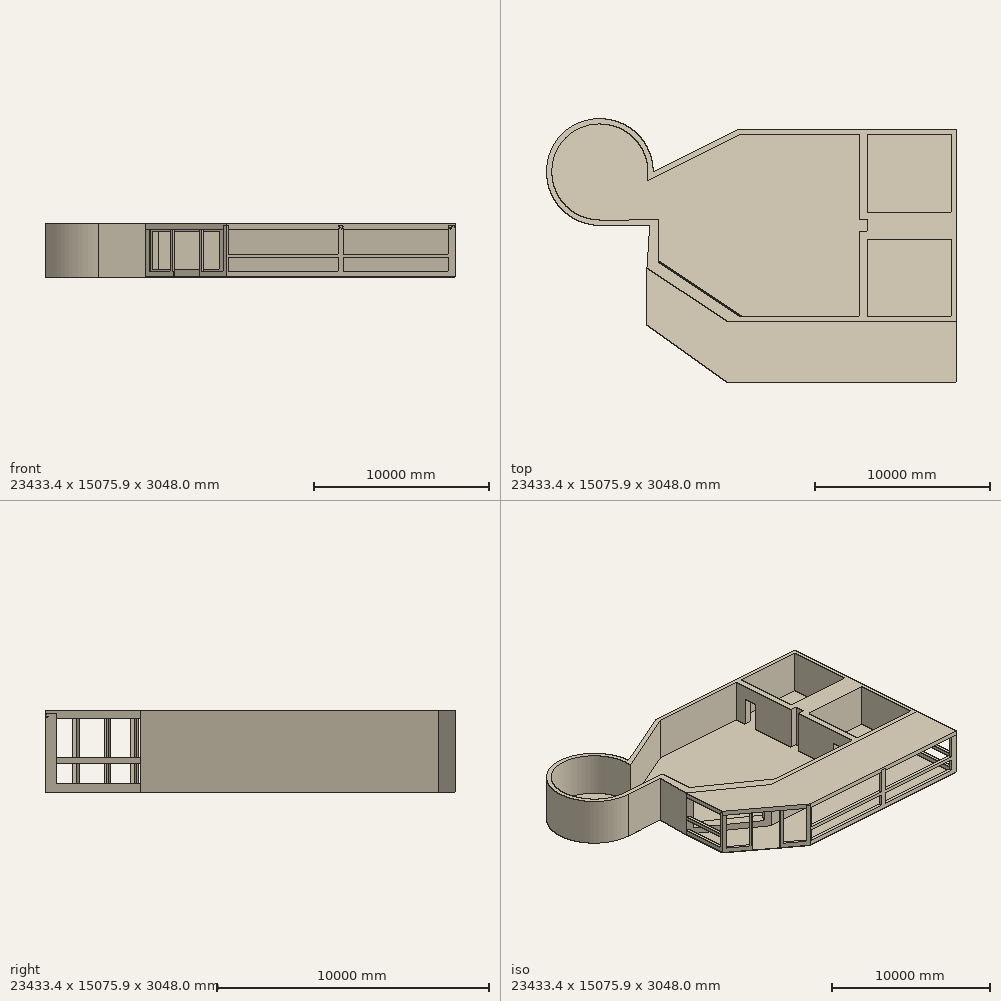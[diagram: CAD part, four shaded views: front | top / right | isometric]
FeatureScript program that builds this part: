
annotation { "Feature Type Name" : "Feature", "Feature Type Description" : "" }
export const myFeature = defineFeature(function(context is Context, id is Id, definition is map)
    precondition{}
    {
        {
            var Q0;
            Q0=qCreatedBy(makeId("Top.planeOp"),FACE);
            var sketch = newSketch(context, id + "F0", { "sketchPlane" : qUnion([Q0])});
            skArc(sketch, "E0", {"start": v(3050.46, 1.82) * mm, "mid": v(-2159.4, 2154.62) * mm, "end": v(4.93, -3050.46) * mm});
            skLineSegment(sketch, "E1", {"start": v(0, -3050.47) * mm, "end": v(2848.18, -3048.16) * mm});
            skPoint(sketch, "E2.start.orphan", {"position": v(-3048, 0) * mm});
            skLineSegment(sketch, "E3.2", {"start": v(7272.16, -8535.97) * mm, "end": v(2693.36, -5490.75) * mm});
            skLineSegment(sketch, "E3.3", {"start": v(2693.36, -5490.75) * mm, "end": v(2848.18, -3048.16) * mm});
            skLineSegment(sketch, "E3.4", {"start": v(3041.2, -2.78) * mm, "end": v(7967.84, 2439.97) * mm});
            skPoint(sketch, "E3.0.midPoint", {"position": v(12372.72, -3349.24) * mm});
            skLineSegment(sketch, "E4", {"start": v(7967.84, 2439.97) * mm, "end": v(20382.9, 2439.97) * mm});
            skLineSegment(sketch, "E5", {"start": v(20382.9, 2439.97) * mm, "end": v(20382.9, -8535.97) * mm});
            skLineSegment(sketch, "E6", {"start": v(20382.9, -8535.97) * mm, "end": v(7272.16, -8535.97) * mm});
            skPoint(sketch, "E7.orphan", {"position": v(12546.64, -605.25) * mm});
            skPoint(sketch, "E3.1.start.orphan", {"position": v(12198.8, -6093.22) * mm});
            skSolve(sketch);
        }
        {
            var Q0;
            Q0 = qSketchRegion(id + "F0", true);
            extrude(context, id + "F1", {"entities" : qUnion([Q0]), "depth" : 3048 * mm, "offsetDistance" : 30.48 * mm});
        }
        {
            var Q0;
            Q0=makeQuery(id+"F1.opExtrude","CAP_FACE",FACE,{"disambiguationData":[OSD([sQuery(id+"F0.wireOp",EDGE,"E0"),sQuery(id+"F0.wireOp",EDGE,"E1"),sQuery(id+"F0.wireOp",EDGE,"E3.2"),sQuery(id+"F0.wireOp",EDGE,"E3.3"),sQuery(id+"F0.wireOp",EDGE,"E3.4"),sQuery(id+"F0.wireOp",EDGE,"E4"),sQuery(id+"F0.wireOp",EDGE,"E5"),sQuery(id+"F0.wireOp",EDGE,"E6")])],"isStart":false});
            var sketch = newSketch(context, id + "F2", { "sketchPlane" : qUnion([Q0])});
            skCircle(sketch, "E8", {"center": v(0, 0) * mm, "radius": 2745.67 * mm});
            skLineSegment(sketch, "E9", {"start": v(2697.21, -513.54) * mm, "end": v(8039.25, 2135.17) * mm});
            skLineSegment(sketch, "E10", {"start": v(8039.25, 2135.17) * mm, "end": v(20078.1, 2135.17) * mm});
            skLineSegment(sketch, "E11", {"start": v(20078.1, 2135.17) * mm, "end": v(20078.1, -8231.17) * mm});
            skLineSegment(sketch, "E12", {"start": v(20078.1, -8231.17) * mm, "end": v(7967.84, -8231.17) * mm});
            skLineSegment(sketch, "E13", {"start": v(7967.84, -8231.17) * mm, "end": v(3324.87, -5143.27) * mm});
            skLineSegment(sketch, "E14", {"start": v(3324.87, -5143.27) * mm, "end": v(3324.87, -2742.98) * mm});
            skLineSegment(sketch, "E15", {"start": v(3324.87, -2742.98) * mm, "end": v(4.93, -2745.66) * mm});
            skSolve(sketch);
        }
        {
            var Q0;
            {var subQ0=sQuery(id+"F2.wireOp",EDGE,"E9");Q0=makeQuery(id+"F2.imprint","IMPRINT",FACE,{"disambiguationData":[TD([[makeQuery(id+"F2.imprint","IMPRINT",EDGE,{"derivedFrom":subQ0}),-1.0]])]});}
            var Q1;
            {var subQ0=sQuery(id+"F2.wireOp",EDGE,"E8");var subQ1=makeQuery(id+"F2.imprint","INTERSECT",VERTEX,{"derivedFrom":[subQ0,sQuery(id+"F2.wireOp",EDGE,"E9")]});Q1=makeQuery(id+"F2.imprint","IMPRINT",FACE,{"disambiguationData":[TD([[makeQuery(id+"F2.imprint","IMPRINT",EDGE,{"disambiguationData":[TD([[subQ1,1.0]])],"derivedFrom":subQ0}),1.0]])]});}
            extrude(context, id + "F3", {"entities" : qUnion([Q0, Q1]), "operationType" : NewBodyOperationType.REMOVE, "oppositeDirection" : true, "depth" : 2743.2 * mm, "offsetDistance" : 30.48 * mm});
        }
        {
            var Q0;
            Q0=makeQuery(id+"F1.opExtrude","SWEPT_FACE",FACE,{"disambiguationData":[OSD([sQuery(id+"F0.wireOp",EDGE,"E3.2")])]});
            var sketch = newSketch(context, id + "F4", { "sketchPlane" : qUnion([Q0])});
            skLineSegment(sketch, "E16.bottom", {"start": v(5740.52, 2590.8) * mm, "end": v(10325.1, 2590.8) * mm});
            skLineSegment(sketch, "E16.top", {"start": v(5740.52, 457.2) * mm, "end": v(10325.1, 457.2) * mm});
            skLineSegment(sketch, "E16.left", {"start": v(5740.52, 2590.8) * mm, "end": v(5740.52, 457.2) * mm});
            skLineSegment(sketch, "E16.right", {"start": v(10325.1, 2590.8) * mm, "end": v(10325.1, 457.2) * mm});
            skSolve(sketch);
        }
        {
            var Q0;
            Q0 = qSketchRegion(id + "F4", true);
            extrude(context, id + "F5", {"entities" : qUnion([Q0]), "operationType" : NewBodyOperationType.REMOVE, "oppositeDirection" : true, "depth" : 914.4 * mm, "offsetDistance" : 30.48 * mm});
        }
        {
            var Q0;
            Q0=makeQuery(id+"F3.boolean.opBoolean","COPY",FACE,{"derivedFrom":makeQuery(id+"F3.opExtrude","SWEPT_FACE",FACE,{"disambiguationData":[OSD([sQuery(id+"F2.wireOp",EDGE,"E13")])]})});
            var sketch = newSketch(context, id + "F6", { "sketchPlane" : qUnion([Q0])});
            skLineSegment(sketch, "E17.bottom", {"start": v(-5616.74, 304.8) * mm, "end": v(-11192.78, 304.8) * mm});
            skLineSegment(sketch, "E17.top", {"start": v(-5616.74, 457.2) * mm, "end": v(-11192.78, 457.2) * mm});
            skLineSegment(sketch, "E17.left", {"start": v(-5616.74, 304.8) * mm, "end": v(-5616.74, 457.2) * mm});
            skLineSegment(sketch, "E17.right", {"start": v(-11192.78, 304.8) * mm, "end": v(-11192.78, 457.2) * mm});
            skSolve(sketch);
        }
        {
            var Q0;
            Q0 = qSketchRegion(id + "F6", true);
            extrude(context, id + "F7", {"entities" : qUnion([Q0]), "operationType" : NewBodyOperationType.ADD, "depth" : 60.96 * mm, "offsetDistance" : 30.48 * mm});
        }
        {
            var Q0;
            Q0=makeQuery(id+"F7.opExtrude","SWEPT_FACE",FACE,{"disambiguationData":[OSD([sQuery(id+"F6.wireOp",EDGE,"E17.right")])]});
            var sketch = newSketch(context, id + "F8", { "sketchPlane" : qUnion([Q0])});
            skLineSegment(sketch, "E18.bottom", {"start": v(-2380.41, 457.2) * mm, "end": v(-2441.37, 457.2) * mm});
            skLineSegment(sketch, "E18.top", {"start": v(-2380.41, 304.8) * mm, "end": v(-2441.37, 304.8) * mm});
            skLineSegment(sketch, "E18.left", {"start": v(-2380.41, 457.2) * mm, "end": v(-2380.41, 304.8) * mm});
            skLineSegment(sketch, "E18.right", {"start": v(-2441.37, 457.2) * mm, "end": v(-2441.37, 304.8) * mm});
            skSolve(sketch);
        }
        {
            var Q0;
            Q0 = qSketchRegion(id + "F8", true);
            extrude(context, id + "F9", {"entities" : qUnion([Q0]), "operationType" : NewBodyOperationType.ADD, "depth" : 91.44 * mm, "offsetDistance" : 30.48 * mm});
        }
        {
            var Q0;
            Q0=makeQuery(id+"F1.opExtrude","CAP_FACE",FACE,{"disambiguationData":[OSD([sQuery(id+"F0.wireOp",EDGE,"E0"),sQuery(id+"F0.wireOp",EDGE,"E1"),sQuery(id+"F0.wireOp",EDGE,"E3.2"),sQuery(id+"F0.wireOp",EDGE,"E3.3"),sQuery(id+"F0.wireOp",EDGE,"E3.4"),sQuery(id+"F0.wireOp",EDGE,"E4"),sQuery(id+"F0.wireOp",EDGE,"E5"),sQuery(id+"F0.wireOp",EDGE,"E6")])],"isStart":true});
            var sketch = newSketch(context, id + "F10", { "sketchPlane" : qUnion([Q0])});
            skLineSegment(sketch, "E19.top", {"start": v(7272.16, 12025.4) * mm, "end": v(20382.9, 12025.4) * mm});
            skLineSegment(sketch, "E19.left", {"start": v(2693.36, 5490.75) * mm, "end": v(2693.36, 8758.07) * mm});
            skLineSegment(sketch, "E19.right", {"start": v(20382.9, 8535.97) * mm, "end": v(20382.9, 12025.4) * mm});
            skLineSegment(sketch, "E20", {"start": v(2693.36, 5490.75) * mm, "end": v(7272.16, 8535.97) * mm});
            skLineSegment(sketch, "E21", {"start": v(7272.16, 8535.97) * mm, "end": v(20382.9, 8535.97) * mm});
            skLineSegment(sketch, "E22", {"start": v(2693.36, 8758.07) * mm, "end": v(7272.16, 12025.4) * mm});
            skPoint(sketch, "E23.orphan", {"position": v(2693.36, 12025.4) * mm});
            skSolve(sketch);
        }
        {
            var Q0;
            Q0 = qSketchRegion(id + "F10", true);
            extrude(context, id + "F11", {"entities" : qUnion([Q0]), "oppositeDirection" : true, "depth" : 30.48 * mm, "offsetDistance" : 30.48 * mm});
        }
        {
            var Q0;
            Q0=makeQuery(id+"F11.opExtrude","CAP_FACE",FACE,{"disambiguationData":[OSD([sQuery(id+"F10.wireOp",EDGE,"E19.top"),sQuery(id+"F10.wireOp",EDGE,"E19.left"),sQuery(id+"F10.wireOp",EDGE,"E19.right"),sQuery(id+"F10.wireOp",EDGE,"E20"),sQuery(id+"F10.wireOp",EDGE,"E21"),sQuery(id+"F10.wireOp",EDGE,"E22")])],"isStart":false});
            var sketch = newSketch(context, id + "F12", { "sketchPlane" : qUnion([Q0])});
            skLineSegment(sketch, "E24", {"start": v(7272.16, -11812.03) * mm, "end": v(20169.55, -11812.03) * mm});
            skLineSegment(sketch, "E25", {"start": v(20169.55, -11812.03) * mm, "end": v(20169.55, -8535.97) * mm});
            skLineSegment(sketch, "E26", {"start": v(2906.72, -5632.65) * mm, "end": v(2906.72, -8696.96) * mm});
            skLineSegment(sketch, "E27", {"start": v(2906.72, -8696.96) * mm, "end": v(7272.16, -11812.03) * mm});
            skSolve(sketch);
        }
        {
            var Q0;
            Q0 = qSketchRegion(id + "F12", true);
            var Q1;
            Q1=makeQuery(id+"F12.imprint","IMPRINT",FACE,{"disambiguationData":[TD([[makeQuery(id+"F12.imprint","IMPRINT",EDGE,{"derivedFrom":sQuery(id+"F12.wireOp",EDGE,"E24")}),-1.0]])]});
            extrude(context, id + "F13", {"entities" : qUnion([Q0, Q1]), "depth" : 304.8 * mm, "offsetDistance" : 30.48 * mm});
        }
        {
            var Q0;
            Q0=makeQuery(id+"F13.opExtrude","SWEPT_FACE",FACE,{"disambiguationData":[OSD([sQuery(id+"F10.wireOp",EDGE,"E22")])]});
            var sketch = newSketch(context, id + "F14", { "sketchPlane" : qUnion([Q0])});
            skLineSegment(sketch, "E28.bottom", {"start": v(10959.47, 30.48) * mm, "end": v(9224.72, 30.48) * mm});
            skLineSegment(sketch, "E28.top", {"start": v(10959.47, 640.08) * mm, "end": v(9224.72, 640.08) * mm});
            skLineSegment(sketch, "E28.left", {"start": v(10959.47, 30.48) * mm, "end": v(10959.47, 640.08) * mm});
            skLineSegment(sketch, "E28.right", {"start": v(9224.72, 30.48) * mm, "end": v(9224.72, 640.08) * mm});
            skPoint(sketch, "E28.middle", {"position": v(10092.1, 335.28) * mm});
            skSolve(sketch);
        }
        {
            var Q0;
            Q0 = qSketchRegion(id + "F14", true);
            extrude(context, id + "F15", {"entities" : qUnion([Q0]), "operationType" : NewBodyOperationType.REMOVE, "oppositeDirection" : true, "depth" : 609.6 * mm, "offsetDistance" : 30.48 * mm});
        }
        {
            var Q0;
            Q0=makeQuery(id+"F15.boolean.opBoolean","COPY",EDGE,{"derivedFrom":makeQuery(id+"F15.opExtrude","CAP_EDGE",EDGE,{"disambiguationData":[OSD([sQuery(id+"F14.wireOp",EDGE,"E28.right")])],"isStart":true})});
            var Q1;
            Q1=makeQuery(id+"F15.boolean.opBoolean","INTERSECT",EDGE,{"derivedFrom":[makeQuery(id+"F13.opExtrude","SWEPT_FACE",FACE,{"disambiguationData":[OSD([sQuery(id+"F12.wireOp",EDGE,"E27")])]}),makeQuery(id+"F15.opExtrude","SWEPT_FACE",FACE,{"disambiguationData":[OSD([sQuery(id+"F14.wireOp",EDGE,"E28.right")])]})]});
            var Q2;
            Q2=makeQuery(id+"F15.boolean.opBoolean","COPY",EDGE,{"derivedFrom":makeQuery(id+"F15.opExtrude","CAP_EDGE",EDGE,{"disambiguationData":[OSD([sQuery(id+"F14.wireOp",EDGE,"E28.left")])],"isStart":true})});
            var Q3;
            Q3=makeQuery(id+"F15.boolean.opBoolean","INTERSECT",EDGE,{"derivedFrom":[makeQuery(id+"F13.opExtrude","SWEPT_FACE",FACE,{"disambiguationData":[OSD([sQuery(id+"F12.wireOp",EDGE,"E27")])]}),makeQuery(id+"F15.opExtrude","SWEPT_FACE",FACE,{"disambiguationData":[OSD([sQuery(id+"F14.wireOp",EDGE,"E28.left")])]})]});
            chamfer(context, id + "F16", {"entities" : qUnion([Q0, Q1, Q2, Q3]), "width" : 60.96 * mm, "tangentPropagation" : true});
        }
        {
            var Q0;
            {var subQ0=sQuery(id+"F10.wireOp",EDGE,"E19.left");var subQ1=sQuery(id+"F12.wireOp",EDGE,"E27");var subQ2=sQuery(id+"F10.wireOp",EDGE,"E22");var subQ3=sQuery(id+"F12.wireOp",EDGE,"E26");var subQ4=sQuery(id+"F10.wireOp",EDGE,"E20");Q0=makeQuery(id+"F15.boolean.opBoolean","SPLIT",FACE,{"disambiguationData":[TD([makeQuery(id+"F13.opExtrude","SWEPT_FACE",FACE,{"disambiguationData":[OSD([subQ3])]})])],"derivedFrom":makeQuery(id+"F13.opExtrude","CAP_FACE",FACE,{"disambiguationData":[OSD([sQuery(id+"F10.wireOp",EDGE,"E19.top"),subQ0,sQuery(id+"F10.wireOp",EDGE,"E19.right"),subQ4,sQuery(id+"F10.wireOp",EDGE,"E21"),subQ2,sQuery(id+"F12.wireOp",EDGE,"E24"),sQuery(id+"F12.wireOp",EDGE,"E25"),subQ3,subQ1])],"isStart":false})});}
            var sketch = newSketch(context, id + "F17", { "sketchPlane" : qUnion([Q0])});
            skLineSegment(sketch, "E29", {"start": v(2906.72, -8600.91) * mm, "end": v(2693.36, -8600.91) * mm});
            skLineSegment(sketch, "E30", {"start": v(2976.84, -8747) * mm, "end": v(2875.95, -8888.37) * mm});
            skLineSegment(sketch, "E31", {"start": v(2875.95, -8888.37) * mm, "end": v(2693.36, -8758.07) * mm});
            skLineSegment(sketch, "E32", {"start": v(2693.36, -8758.07) * mm, "end": v(2693.36, -8600.91) * mm});
            skLineSegment(sketch, "E33", {"start": v(2906.72, -8600.91) * mm, "end": v(2906.72, -8696.96) * mm});
            skLineSegment(sketch, "E34", {"start": v(2906.72, -8696.96) * mm, "end": v(2976.84, -8747) * mm});
            skLineSegment(sketch, "E35", {"start": v(4103.04, -9763.98) * mm, "end": v(4203.92, -9622.6) * mm});
            skLineSegment(sketch, "E36", {"start": v(4203.92, -9622.6) * mm, "end": v(4327.97, -9711.13) * mm});
            skLineSegment(sketch, "E37", {"start": v(4327.97, -9711.13) * mm, "end": v(4342.18, -9796.16) * mm});
            skLineSegment(sketch, "E38", {"start": v(4342.18, -9796.16) * mm, "end": v(4312.12, -9838.29) * mm});
            skLineSegment(sketch, "E39", {"start": v(4312.12, -9838.29) * mm, "end": v(4227.1, -9852.5) * mm});
            skLineSegment(sketch, "E40", {"start": v(4227.1, -9852.5) * mm, "end": v(4103.04, -9763.98) * mm});
            skSolve(sketch);
        }
        {
            var Q0;
            Q0 = qSketchRegion(id + "F17", true);
            extrude(context, id + "F18", {"entities" : qUnion([Q0]), "operationType" : NewBodyOperationType.ADD, "depth" : 2590.8 * mm, "offsetDistance" : 30.48 * mm});
        }
        {
            var Q0;
            {var subQ0=sQuery(id+"F10.wireOp",EDGE,"E19.top");var subQ1=sQuery(id+"F12.wireOp",EDGE,"E25");var subQ2=sQuery(id+"F12.wireOp",EDGE,"E27");var subQ3=sQuery(id+"F12.wireOp",EDGE,"E24");var subQ4=sQuery(id+"F10.wireOp",EDGE,"E21");var subQ5=sQuery(id+"F10.wireOp",EDGE,"E19.right");var subQ6=sQuery(id+"F10.wireOp",EDGE,"E22");Q0=makeQuery(id+"F15.boolean.opBoolean","SPLIT",FACE,{"disambiguationData":[TD([makeQuery(id+"F13.opExtrude","SWEPT_FACE",FACE,{"disambiguationData":[OSD([subQ3])]})])],"derivedFrom":makeQuery(id+"F13.opExtrude","CAP_FACE",FACE,{"disambiguationData":[OSD([subQ0,sQuery(id+"F10.wireOp",EDGE,"E19.left"),subQ5,sQuery(id+"F10.wireOp",EDGE,"E20"),subQ4,subQ6,subQ3,subQ1,sQuery(id+"F12.wireOp",EDGE,"E26"),subQ2])],"isStart":false})});}
            var sketch = newSketch(context, id + "F19", { "sketchPlane" : qUnion([Q0])});
            skLineSegment(sketch, "E41", {"start": v(5963.37, -10878.1) * mm, "end": v(5862.49, -11019.48) * mm});
            skLineSegment(sketch, "E42", {"start": v(5862.49, -11019.48) * mm, "end": v(5738.43, -10930.96) * mm});
            skLineSegment(sketch, "E43", {"start": v(5738.43, -10930.96) * mm, "end": v(5724.22, -10845.93) * mm});
            skLineSegment(sketch, "E44", {"start": v(5724.22, -10845.93) * mm, "end": v(5754.28, -10803.8) * mm});
            skLineSegment(sketch, "E45", {"start": v(5754.28, -10803.8) * mm, "end": v(5839.31, -10789.58) * mm});
            skLineSegment(sketch, "E46", {"start": v(5839.31, -10789.58) * mm, "end": v(5963.37, -10878.1) * mm});
            skLineSegment(sketch, "E47", {"start": v(7201.78, -11761.8) * mm, "end": v(7100.9, -11903.18) * mm});
            skLineSegment(sketch, "E48", {"start": v(7100.9, -11903.18) * mm, "end": v(7272.16, -12025.4) * mm});
            skLineSegment(sketch, "E49", {"start": v(7272.16, -12025.4) * mm, "end": v(7382.18, -12025.4) * mm});
            skLineSegment(sketch, "E50", {"start": v(7382.18, -12025.4) * mm, "end": v(7382.18, -11812.03) * mm});
            skLineSegment(sketch, "E51", {"start": v(7382.18, -11812.03) * mm, "end": v(7272.16, -11812.03) * mm});
            skLineSegment(sketch, "E52", {"start": v(7272.16, -11812.03) * mm, "end": v(7201.78, -11761.8) * mm});
            skLineSegment(sketch, "E53", {"start": v(19960.46, -11812.03) * mm, "end": v(19960.46, -12025.4) * mm});
            skLineSegment(sketch, "E54", {"start": v(19960.46, -12025.4) * mm, "end": v(20382.9, -12025.4) * mm});
            skLineSegment(sketch, "E55", {"start": v(20382.9, -12025.4) * mm, "end": v(20382.9, -11633.8) * mm});
            skLineSegment(sketch, "E56", {"start": v(20382.9, -11633.8) * mm, "end": v(20169.55, -11633.8) * mm});
            skLineSegment(sketch, "E57", {"start": v(20169.55, -11633.8) * mm, "end": v(20169.55, -11812.03) * mm});
            skLineSegment(sketch, "E58", {"start": v(20169.55, -11812.03) * mm, "end": v(19960.46, -11812.03) * mm});
            skLineSegment(sketch, "E59", {"start": v(13827.54, -12025.4) * mm, "end": v(13668.18, -12025.4) * mm});
            skLineSegment(sketch, "E60", {"start": v(13668.18, -12025.4) * mm, "end": v(13668.18, -11812.03) * mm});
            skLineSegment(sketch, "E61", {"start": v(13668.18, -11812.03) * mm, "end": v(13985.48, -11812.03) * mm});
            skLineSegment(sketch, "E62", {"start": v(13985.48, -11812.03) * mm, "end": v(13985.48, -12025.4) * mm});
            skLineSegment(sketch, "E63", {"start": v(13985.48, -12025.4) * mm, "end": v(13827.54, -12025.4) * mm});
            skSolve(sketch);
        }
        {
            var Q0;
            Q0=makeQuery(id+"F19.imprint","IMPRINT",FACE,{"disambiguationData":[TD([[makeQuery(id+"F19.imprint","IMPRINT",EDGE,{"derivedFrom":sQuery(id+"F19.wireOp",EDGE,"E59")}),1.0]])]});
            var Q1;
            Q1=makeQuery(id+"F19.imprint","IMPRINT",FACE,{"disambiguationData":[TD([[makeQuery(id+"F19.imprint","IMPRINT",EDGE,{"derivedFrom":sQuery(id+"F19.wireOp",EDGE,"E53")}),1.0]])]});
            var Q2;
            Q2=makeQuery(id+"F19.imprint","IMPRINT",FACE,{"disambiguationData":[TD([[makeQuery(id+"F19.imprint","IMPRINT",EDGE,{"derivedFrom":sQuery(id+"F19.wireOp",EDGE,"E41")}),-1.0]])]});
            var Q3;
            Q3=makeQuery(id+"F19.imprint","IMPRINT",FACE,{"disambiguationData":[TD([[makeQuery(id+"F19.imprint","IMPRINT",EDGE,{"derivedFrom":sQuery(id+"F19.wireOp",EDGE,"E47")}),1.0]])]});
            extrude(context, id + "F20", {"entities" : qUnion([Q0, Q1, Q2, Q3]), "operationType" : NewBodyOperationType.ADD, "depth" : 2590.8 * mm, "offsetDistance" : 30.48 * mm});
        }
        {
            var Q0;
            Q0=makeQuery(id+"F1.opExtrude","CAP_FACE",FACE,{"disambiguationData":[OSD([sQuery(id+"F0.wireOp",EDGE,"E0"),sQuery(id+"F0.wireOp",EDGE,"E1"),sQuery(id+"F0.wireOp",EDGE,"E3.2"),sQuery(id+"F0.wireOp",EDGE,"E3.3"),sQuery(id+"F0.wireOp",EDGE,"E3.4"),sQuery(id+"F0.wireOp",EDGE,"E4"),sQuery(id+"F0.wireOp",EDGE,"E5"),sQuery(id+"F0.wireOp",EDGE,"E6")])],"isStart":false});
            var sketch = newSketch(context, id + "F21", { "sketchPlane" : qUnion([Q0])});
            skLineSegment(sketch, "E64", {"start": v(2693.36, -5490.75) * mm, "end": v(2693.36, -8758.07) * mm});
            skLineSegment(sketch, "E65", {"start": v(2693.36, -8758.07) * mm, "end": v(7272.16, -12025.4) * mm});
            skLineSegment(sketch, "E66", {"start": v(7272.16, -12025.4) * mm, "end": v(20382.9, -12025.4) * mm});
            skLineSegment(sketch, "E67", {"start": v(20382.9, -12025.4) * mm, "end": v(20382.9, -8535.97) * mm});
            skLineSegment(sketch, "E68", {"start": v(20382.9, -8535.97) * mm, "end": v(7272.16, -8535.97) * mm});
            skLineSegment(sketch, "E69", {"start": v(7272.16, -8535.97) * mm, "end": v(2693.36, -5490.75) * mm});
            skSolve(sketch);
        }
        {
            var Q0;
            Q0 = qSketchRegion(id + "F21", true);
            extrude(context, id + "F22", {"entities" : qUnion([Q0]), "oppositeDirection" : true, "depth" : 304.8 * mm, "offsetDistance" : 30.48 * mm});
        }
        {
            var Q0;
            Q0=makeQuery(id+"F20.opExtrude","SWEPT_FACE",FACE,{"disambiguationData":[OSD([sQuery(id+"F19.wireOp",EDGE,"E56")])]});
            var sketch = newSketch(context, id + "F23", { "sketchPlane" : qUnion([Q0])});
            skLineSegment(sketch, "E70.bottom", {"start": v(-20169.55, 1097.28) * mm, "end": v(-20382.9, 1097.28) * mm});
            skLineSegment(sketch, "E70.top", {"start": v(-20169.55, 1310.64) * mm, "end": v(-20382.9, 1310.64) * mm});
            skLineSegment(sketch, "E70.left", {"start": v(-20169.55, 1097.28) * mm, "end": v(-20169.55, 1310.64) * mm});
            skLineSegment(sketch, "E70.right", {"start": v(-20382.9, 1097.28) * mm, "end": v(-20382.9, 1310.64) * mm});
            skSolve(sketch);
        }
        {
            var Q0;
            Q0 = qSketchRegion(id + "F23", true);
            extrude(context, id + "F24", {"entities" : qUnion([Q0]), "endBound" : BoundingType.UP_TO_NEXT, "depth" : 30.48 * mm, "offsetDistance" : 30.48 * mm});
        }
        {
            var Q0;
            Q0=makeQuery(id+"F20.opExtrude","SWEPT_FACE",FACE,{"disambiguationData":[OSD([sQuery(id+"F19.wireOp",EDGE,"E62")])]});
            var sketch = newSketch(context, id + "F25", { "sketchPlane" : qUnion([Q0])});
            skLineSegment(sketch, "E71.bottom", {"start": v(-12025.4, 1097.28) * mm, "end": v(-11812.03, 1097.28) * mm});
            skLineSegment(sketch, "E71.top", {"start": v(-12025.4, 1310.64) * mm, "end": v(-11812.03, 1310.64) * mm});
            skLineSegment(sketch, "E71.left", {"start": v(-12025.4, 1097.28) * mm, "end": v(-12025.4, 1310.64) * mm});
            skLineSegment(sketch, "E71.right", {"start": v(-11812.03, 1097.28) * mm, "end": v(-11812.03, 1310.64) * mm});
            skSolve(sketch);
        }
        {
            var Q0;
            Q0 = qSketchRegion(id + "F25", true);
            extrude(context, id + "F26", {"entities" : qUnion([Q0]), "operationType" : NewBodyOperationType.ADD, "endBound" : BoundingType.UP_TO_NEXT, "depth" : 30.48 * mm, "offsetDistance" : 30.48 * mm});
        }
        {
            var Q0;
            Q0=makeQuery(id+"F20.opExtrude","SWEPT_FACE",FACE,{"disambiguationData":[OSD([sQuery(id+"F19.wireOp",EDGE,"E60")])]});
            var sketch = newSketch(context, id + "F27", { "sketchPlane" : qUnion([Q0])});
            skLineSegment(sketch, "E72.bottom", {"start": v(12025.4, 1310.64) * mm, "end": v(11812.03, 1310.64) * mm});
            skLineSegment(sketch, "E72.top", {"start": v(12025.4, 1097.28) * mm, "end": v(11812.03, 1097.28) * mm});
            skLineSegment(sketch, "E72.left", {"start": v(12025.4, 1310.64) * mm, "end": v(12025.4, 1097.28) * mm});
            skLineSegment(sketch, "E72.right", {"start": v(11812.03, 1310.64) * mm, "end": v(11812.03, 1097.28) * mm});
            skSolve(sketch);
        }
        {
            var Q0;
            Q0 = qSketchRegion(id + "F27", true);
            extrude(context, id + "F28", {"entities" : qUnion([Q0]), "operationType" : NewBodyOperationType.ADD, "endBound" : BoundingType.UP_TO_NEXT, "depth" : 30.48 * mm, "offsetDistance" : 30.48 * mm});
        }
        {
            var Q0;
            Q0=makeQuery(id+"F18.opExtrude","SWEPT_FACE",FACE,{"disambiguationData":[OSD([sQuery(id+"F17.wireOp",EDGE,"E29")])]});
            var sketch = newSketch(context, id + "F29", { "sketchPlane" : qUnion([Q0])});
            skLineSegment(sketch, "E73.bottom", {"start": v(-2693.36, 1097.28) * mm, "end": v(-2906.72, 1097.28) * mm});
            skLineSegment(sketch, "E73.top", {"start": v(-2693.36, 1310.64) * mm, "end": v(-2906.72, 1310.64) * mm});
            skLineSegment(sketch, "E73.left", {"start": v(-2693.36, 1097.28) * mm, "end": v(-2693.36, 1310.64) * mm});
            skLineSegment(sketch, "E73.right", {"start": v(-2906.72, 1097.28) * mm, "end": v(-2906.72, 1310.64) * mm});
            skSolve(sketch);
        }
        {
            var Q0;
            Q0 = qSketchRegion(id + "F29", true);
            extrude(context, id + "F30", {"entities" : qUnion([Q0]), "endBound" : BoundingType.UP_TO_NEXT, "depth" : 30.48 * mm, "offsetDistance" : 30.48 * mm});
        }
        {
            var Q0;
            Q0=makeQuery(id+"F3.boolean.opBoolean","COPY",FACE,{"derivedFrom":makeQuery(id+"F3.opExtrude","CAP_FACE",FACE,{"disambiguationData":[OSD([sQuery(id+"F2.wireOp",EDGE,"E8"),sQuery(id+"F2.wireOp",EDGE,"E9"),sQuery(id+"F2.wireOp",EDGE,"E10"),sQuery(id+"F2.wireOp",EDGE,"E11"),sQuery(id+"F2.wireOp",EDGE,"E12"),sQuery(id+"F2.wireOp",EDGE,"E13"),sQuery(id+"F2.wireOp",EDGE,"E14"),sQuery(id+"F2.wireOp",EDGE,"E15")])],"isStart":false})});
            var sketch = newSketch(context, id + "F31", { "sketchPlane" : qUnion([Q0])});
            skLineSegment(sketch, "E74", {"start": v(14864.6, 2135.17) * mm, "end": v(14864.6, -2742.98) * mm});
            skLineSegment(sketch, "E75", {"start": v(14864.6, -2742.98) * mm, "end": v(20078.1, -2742.98) * mm});
            skLineSegment(sketch, "E76", {"start": v(15291.32, 2135.17) * mm, "end": v(15291.32, -2316.26) * mm});
            skLineSegment(sketch, "E77", {"start": v(15291.32, -2316.26) * mm, "end": v(20078.1, -2316.26) * mm});
            skSolve(sketch);
        }
        {
            var Q0;
            Q0 = qSketchRegion(id + "F31", true);
            var Q1;
            {var subQ1=sQuery(id+"F31.wireOp",EDGE,"E74");Q1=makeQuery(id+"F31.imprint","IMPRINT",FACE,{"disambiguationData":[TD([[makeQuery(id+"F31.imprint","IMPRINT",EDGE,{"derivedFrom":subQ1}),1.0]])]});}
            extrude(context, id + "F32", {"entities" : qUnion([Q0, Q1]), "operationType" : NewBodyOperationType.ADD, "depth" : 2743.2 * mm, "offsetDistance" : 30.48 * mm});
        }
        {
            var Q0;
            {var subQ1=sQuery(id+"F2.wireOp",EDGE,"E15");var subQ2=sQuery(id+"F2.wireOp",EDGE,"E14");var subQ3=sQuery(id+"F2.wireOp",EDGE,"E12");var subQ4=sQuery(id+"F2.wireOp",EDGE,"E8");var subQ6=sQuery(id+"F2.wireOp",EDGE,"E9");var subQ7=sQuery(id+"F2.wireOp",EDGE,"E10");var subQ8=sQuery(id+"F2.wireOp",EDGE,"E11");Q0=makeQuery(id+"F32.boolean.opBoolean","SPLIT",FACE,{"disambiguationData":[TD([makeQuery(id+"F3.boolean.opBoolean","COPY",FACE,{"derivedFrom":makeQuery(id+"F3.opExtrude","SWEPT_FACE",FACE,{"disambiguationData":[OSD([subQ4])]})})])],"derivedFrom":makeQuery(id+"F3.boolean.opBoolean","COPY",FACE,{"derivedFrom":makeQuery(id+"F3.opExtrude","CAP_FACE",FACE,{"disambiguationData":[OSD([subQ4,subQ6,subQ7,subQ8,subQ3,sQuery(id+"F2.wireOp",EDGE,"E13"),subQ2,subQ1])],"isStart":false})})});}
            var sketch = newSketch(context, id + "F33", { "sketchPlane" : qUnion([Q0])});
            skLineSegment(sketch, "E78", {"start": v(14864.6, -3420.19) * mm, "end": v(14864.6, -8231.17) * mm});
            skLineSegment(sketch, "E79", {"start": v(14864.6, -3420.19) * mm, "end": v(20078.1, -3420.19) * mm});
            skLineSegment(sketch, "E80", {"start": v(20078.1, -3420.19) * mm, "end": v(20078.1, -3846.9) * mm});
            skLineSegment(sketch, "E81", {"start": v(20078.1, -3846.9) * mm, "end": v(15291.32, -3846.9) * mm});
            skLineSegment(sketch, "E82", {"start": v(15291.32, -3846.9) * mm, "end": v(15291.32, -8231.17) * mm});
            skSolve(sketch);
        }
        {
            var Q0;
            Q0 = qSketchRegion(id + "F33", true);
            var Q1;
            {var subQ0=sQuery(id+"F33.wireOp",EDGE,"E78");Q1=makeQuery(id+"F33.imprint","IMPRINT",FACE,{"disambiguationData":[TD([[makeQuery(id+"F33.imprint","IMPRINT",EDGE,{"derivedFrom":subQ0}),1.0]])]});}
            extrude(context, id + "F34", {"entities" : qUnion([Q0, Q1]), "operationType" : NewBodyOperationType.ADD, "depth" : 2743.2 * mm, "offsetDistance" : 30.48 * mm});
        }
        {
            var Q0;
            Q0=makeQuery(id+"F34.opExtrude","SWEPT_FACE",FACE,{"disambiguationData":[OSD([sQuery(id+"F33.wireOp",EDGE,"E78")])]});
            var sketch = newSketch(context, id + "F35", { "sketchPlane" : qUnion([Q0])});
            skLineSegment(sketch, "E83.bottom", {"start": v(6554.77, 304.8) * mm, "end": v(7469.17, 304.8) * mm});
            skLineSegment(sketch, "E83.top", {"start": v(6554.77, 2133.6) * mm, "end": v(7469.17, 2133.6) * mm});
            skLineSegment(sketch, "E83.left", {"start": v(6554.77, 304.8) * mm, "end": v(6554.77, 2133.6) * mm});
            skLineSegment(sketch, "E83.right", {"start": v(7469.17, 304.8) * mm, "end": v(7469.17, 2133.6) * mm});
            skSolve(sketch);
        }
        {
            var Q0;
            Q0 = qSketchRegion(id + "F35", true);
            extrude(context, id + "F36", {"entities" : qUnion([Q0]), "operationType" : NewBodyOperationType.REMOVE, "oppositeDirection" : true, "depth" : 914.4 * mm, "offsetDistance" : 30.48 * mm});
        }
        {
            var Q0;
            Q0=makeQuery(id+"F32.opExtrude","SWEPT_FACE",FACE,{"disambiguationData":[OSD([sQuery(id+"F31.wireOp",EDGE,"E74")])]});
            var sketch = newSketch(context, id + "F37", { "sketchPlane" : qUnion([Q0])});
            skLineSegment(sketch, "E84.bottom", {"start": v(-1373.17, 304.8) * mm, "end": v(-458.77, 304.8) * mm});
            skLineSegment(sketch, "E84.top", {"start": v(-1373.17, 2133.6) * mm, "end": v(-458.77, 2133.6) * mm});
            skLineSegment(sketch, "E84.left", {"start": v(-1373.17, 304.8) * mm, "end": v(-1373.17, 2133.6) * mm});
            skLineSegment(sketch, "E84.right", {"start": v(-458.77, 304.8) * mm, "end": v(-458.77, 2133.6) * mm});
            skSolve(sketch);
        }
        {
            var Q0;
            Q0=makeQuery(id+"F37.imprint","IMPRINT",FACE,{"disambiguationData":[TD([[makeQuery(id+"F37.imprint","IMPRINT",EDGE,{"derivedFrom":sQuery(id+"F37.wireOp",EDGE,"E84.bottom")}),1.0]])]});
            extrude(context, id + "F38", {"entities" : qUnion([Q0]), "operationType" : NewBodyOperationType.REMOVE, "oppositeDirection" : true, "depth" : 914.4 * mm, "offsetDistance" : 30.48 * mm});
        }
        {
            var Q0;
            {var subQ0=sQuery(id+"F2.wireOp",EDGE,"E11");var subQ2=sQuery(id+"F2.wireOp",EDGE,"E12");var subQ7=sQuery(id+"F2.wireOp",EDGE,"E15");var subQ9=sQuery(id+"F2.wireOp",EDGE,"E14");var subQ11=sQuery(id+"F2.wireOp",EDGE,"E8");var subQ12=makeQuery(id+"F3.boolean.opBoolean","COPY",FACE,{"derivedFrom":makeQuery(id+"F3.opExtrude","SWEPT_FACE",FACE,{"disambiguationData":[OSD([subQ11])]})});var subQ15=sQuery(id+"F2.wireOp",EDGE,"E9");var subQ17=sQuery(id+"F2.wireOp",EDGE,"E10");var subQ22=makeQuery(id+"F3.boolean.opBoolean","COPY",FACE,{"derivedFrom":makeQuery(id+"F3.opExtrude","CAP_FACE",FACE,{"disambiguationData":[OSD([subQ11,subQ15,subQ17,subQ0,subQ2,sQuery(id+"F2.wireOp",EDGE,"E13"),subQ9,subQ7])],"isStart":false})});var subQ23=makeQuery(id+"F32.boolean.opBoolean","SPLIT",FACE,{"disambiguationData":[TD([subQ12])],"derivedFrom":subQ22});Q0=makeQuery(id+"F38.boolean.opBoolean","MERGE",FACE,{"derivedFrom":[makeQuery(id+"F32.boolean.opBoolean","SPLIT",FACE,{"disambiguationData":[TD([makeQuery(id+"F32.opExtrude","SWEPT_FACE",FACE,{"disambiguationData":[OSD([sQuery(id+"F31.wireOp",EDGE,"E76")])]})])],"derivedFrom":subQ22}),makeQuery(id+"F36.boolean.opBoolean","MERGE",FACE,{"derivedFrom":[makeQuery(id+"F34.boolean.opBoolean","SPLIT",FACE,{"disambiguationData":[TD([subQ12])],"derivedFrom":subQ23}),makeQuery(id+"F34.boolean.opBoolean","SPLIT",FACE,{"disambiguationData":[TD([makeQuery(id+"F34.opExtrude","SWEPT_FACE",FACE,{"disambiguationData":[OSD([sQuery(id+"F33.wireOp",EDGE,"E81")])]})])],"derivedFrom":subQ23}),makeQuery(id+"F36.opExtrude","SWEPT_FACE",FACE,{"disambiguationData":[OSD([sQuery(id+"F35.wireOp",EDGE,"E83.bottom")])]})]}),makeQuery(id+"F38.opExtrude","SWEPT_FACE",FACE,{"disambiguationData":[OSD([sQuery(id+"F37.wireOp",EDGE,"E84.bottom")])]})]});}
            var sketch = newSketch(context, id + "F39", { "sketchPlane" : qUnion([Q0])});
            skLineSegment(sketch, "E85.bottom", {"start": v(15291.32, -3420.19) * mm, "end": v(20078.1, -3420.19) * mm});
            skLineSegment(sketch, "E85.top", {"start": v(15291.32, -2742.98) * mm, "end": v(20078.1, -2742.98) * mm});
            skLineSegment(sketch, "E85.left", {"start": v(15291.32, -3420.19) * mm, "end": v(15291.32, -2742.98) * mm});
            skLineSegment(sketch, "E85.right", {"start": v(20078.1, -3420.19) * mm, "end": v(20078.1, -2742.98) * mm});
            skSolve(sketch);
        }
        {
            var Q0;
            Q0 = qSketchRegion(id + "F39", true);
            extrude(context, id + "F40", {"entities" : qUnion([Q0]), "operationType" : NewBodyOperationType.ADD, "depth" : 2743.2 * mm, "offsetDistance" : 30.48 * mm});
        }
    });
